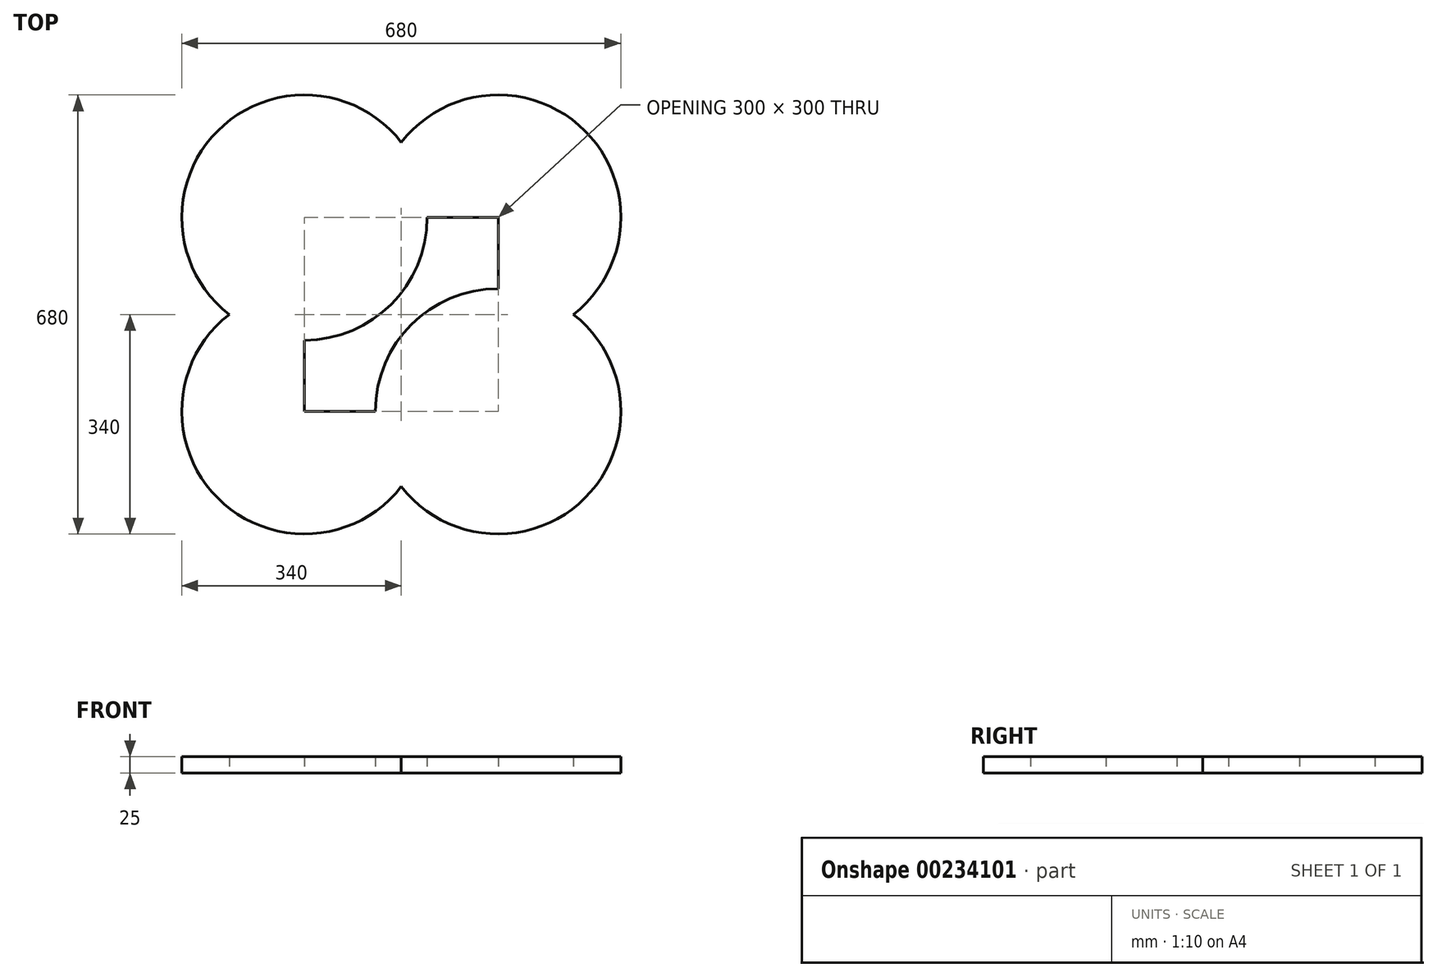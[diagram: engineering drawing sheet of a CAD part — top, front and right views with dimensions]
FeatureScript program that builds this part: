
annotation { "Feature Type Name" : "Feature", "Feature Type Description" : "" }
export const myFeature = defineFeature(function(context is Context, id is Id, definition is map)
    precondition{}
    {
        {
            var Q0;
            Q0=qCreatedBy(makeId("Top.planeOp"),FACE);
            var sketch = newSketch(context, id + "F0", { "sketchPlane" : qUnion([Q0])});
            skLineSegment(sketch, "E0.bottom", {"start": v(-150, -150) * mm, "end": v(150, -150) * mm});
            skLineSegment(sketch, "E0.top", {"start": v(-150, 150) * mm, "end": v(150, 150) * mm});
            skLineSegment(sketch, "E0.left", {"start": v(-150, -150) * mm, "end": v(-150, 150) * mm});
            skLineSegment(sketch, "E0.right", {"start": v(150, -150) * mm, "end": v(150, 150) * mm});
            skPoint(sketch, "E0.middle", {"position": v(0, 0) * mm});
            skCircle(sketch, "E1", {"center": v(-150, 150) * mm, "radius": 190 * mm});
            skCircle(sketch, "E2", {"center": v(150, 150) * mm, "radius": 190 * mm});
            skCircle(sketch, "E3", {"center": v(-150, -150) * mm, "radius": 190 * mm});
            skCircle(sketch, "E4", {"center": v(150, -150) * mm, "radius": 190 * mm});
            skSolve(sketch);
        }
        {
            var Q0;
            Q0 = qSketchRegion(id + "F0", true);
            var Q1;
            {var subQ0=sQuery(id+"F0.wireOp",EDGE,"E2");var subQ1=sQuery(id+"F0.wireOp",EDGE,"E0.top");var subQ2=makeQuery(id+"F0.imprint","INTERSECT",VERTEX,{"derivedFrom":[subQ1,subQ0]});Q1=makeQuery(id+"F0.imprint","IMPRINT",FACE,{"disambiguationData":[TD([[makeQuery(id+"F0.imprint","IMPRINT",EDGE,{"disambiguationData":[TD([[subQ2,-1.0]])],"derivedFrom":subQ1}),-1.0]])]});}
            var Q2;
            {var subQ1=sQuery(id+"F0.wireOp",EDGE,"E0.top");var subQ5=sQuery(id+"F0.wireOp",EDGE,"E0.left");var subQ6=makeQuery(id+"F0.imprint","INTERSECT",VERTEX,{"derivedFrom":[subQ1,subQ5]});Q2=makeQuery(id+"F0.imprint","IMPRINT",FACE,{"disambiguationData":[TD([[makeQuery(id+"F0.imprint","IMPRINT",EDGE,{"disambiguationData":[TD([[subQ6,-1.0]])],"derivedFrom":subQ1}),-1.0]])]});}
            var Q3;
            {var subQ0=sQuery(id+"F0.wireOp",EDGE,"E1");var subQ1=sQuery(id+"F0.wireOp",EDGE,"E0.left");var subQ2=makeQuery(id+"F0.imprint","INTERSECT",VERTEX,{"derivedFrom":[subQ1,subQ0]});Q3=makeQuery(id+"F0.imprint","IMPRINT",FACE,{"disambiguationData":[TD([[makeQuery(id+"F0.imprint","IMPRINT",EDGE,{"disambiguationData":[TD([[subQ2,-1.0]])],"derivedFrom":subQ1}),-1.0]])]});}
            var Q4;
            {var subQ0=sQuery(id+"F0.wireOp",EDGE,"E4");var subQ1=sQuery(id+"F0.wireOp",EDGE,"E0.bottom");var subQ2=makeQuery(id+"F0.imprint","INTERSECT",VERTEX,{"derivedFrom":[subQ1,subQ0]});Q4=makeQuery(id+"F0.imprint","IMPRINT",FACE,{"disambiguationData":[TD([[makeQuery(id+"F0.imprint","IMPRINT",EDGE,{"disambiguationData":[TD([[subQ2,-1.0]])],"derivedFrom":subQ1}),1.0]])]});}
            var Q5;
            {var subQ1=sQuery(id+"F0.wireOp",EDGE,"E0.right");var subQ7=sQuery(id+"F0.wireOp",EDGE,"E0.bottom");var subQ9=makeQuery(id+"F0.imprint","INTERSECT",VERTEX,{"derivedFrom":[subQ7,subQ1]});Q5=makeQuery(id+"F0.imprint","IMPRINT",FACE,{"disambiguationData":[TD([[makeQuery(id+"F0.imprint","IMPRINT",EDGE,{"disambiguationData":[TD([[subQ9,1.0]])],"derivedFrom":subQ7}),1.0]])]});}
            var Q6;
            {var subQ0=sQuery(id+"F0.wireOp",EDGE,"E2");var subQ1=sQuery(id+"F0.wireOp",EDGE,"E0.right");var subQ2=makeQuery(id+"F0.imprint","INTERSECT",VERTEX,{"derivedFrom":[subQ1,subQ0]});Q6=makeQuery(id+"F0.imprint","IMPRINT",FACE,{"disambiguationData":[TD([[makeQuery(id+"F0.imprint","IMPRINT",EDGE,{"disambiguationData":[TD([[subQ2,-1.0]])],"derivedFrom":subQ1}),1.0]])]});}
            extrude(context, id + "F1", {"entities" : qUnion([Q0, Q1, Q2, Q3, Q4, Q5, Q6]), "depth" : 25 * mm});
        }
    });
